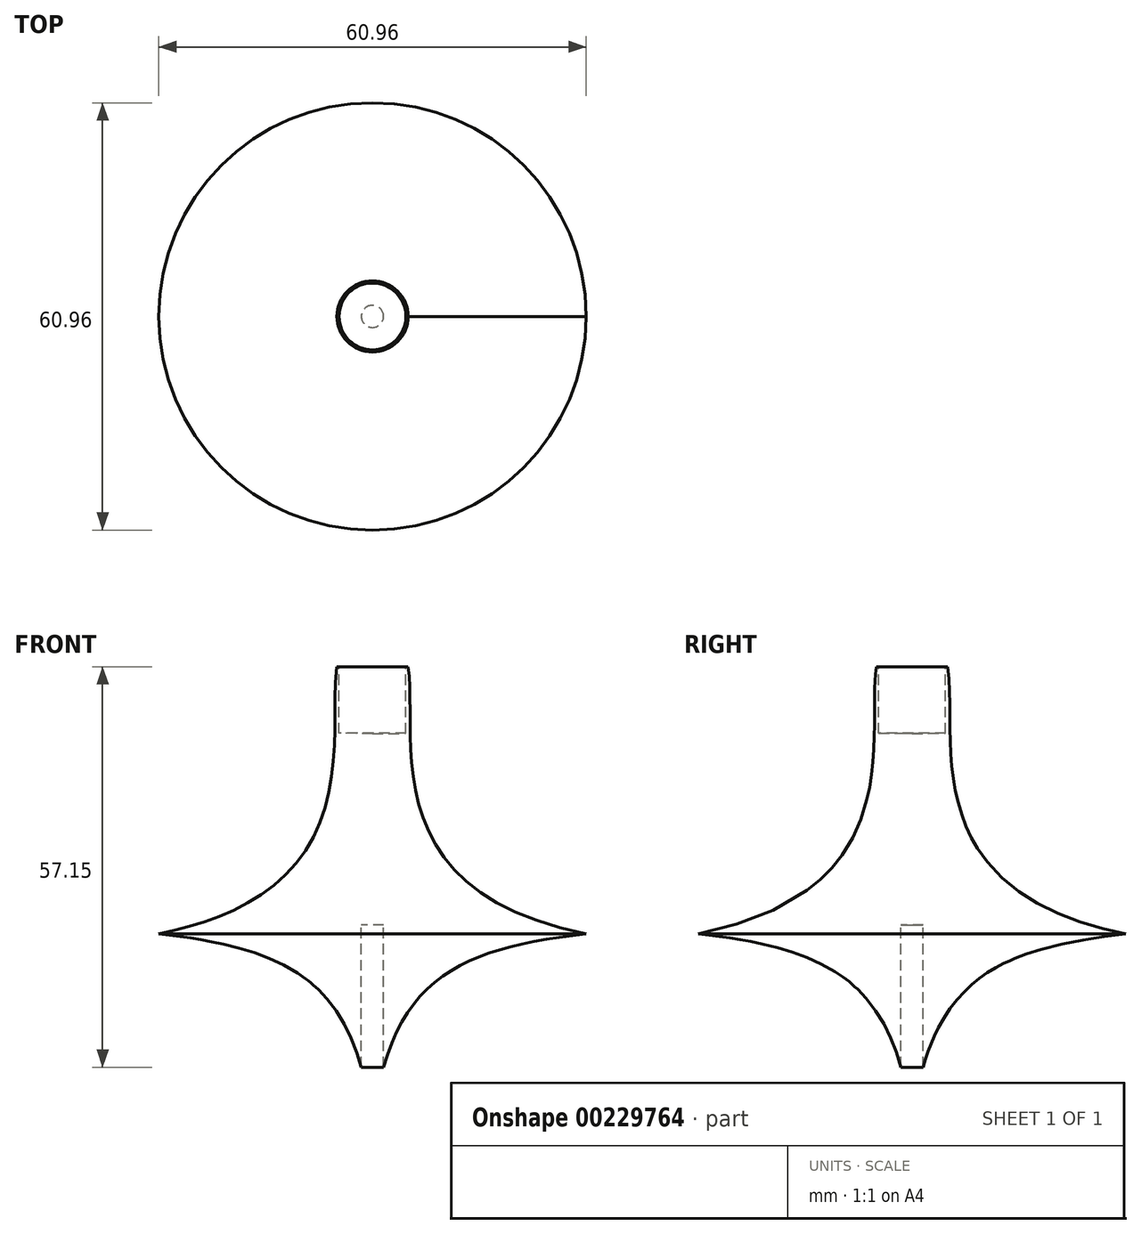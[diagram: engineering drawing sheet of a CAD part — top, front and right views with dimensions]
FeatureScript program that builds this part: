
annotation { "Feature Type Name" : "Feature", "Feature Type Description" : "" }
export const myFeature = defineFeature(function(context is Context, id is Id, definition is map)
    precondition{}
    {
        {
            var Q0;
            Q0=qCreatedBy(makeId("Front.planeOp"),FACE);
            var sketch = newSketch(context, id + "F0", { "sketchPlane" : qUnion([Q0])});
            skLineSegment(sketch, "E0", {"start": v(0, 57.15) * mm, "end": v(0, 0) * mm});
            skFitSpline(sketch, "E1", {"points": [v(5.08, 57.15) * mm, v(30.48, 19.05) * mm], "startDerivative": vector(4.43, -30.47) * mm, "endDerivative": vector(91.44, -18.09) * mm});
            skFitSpline(sketch, "E2", {"points": [v(30.48, 19.05) * mm, v(1.59, 0) * mm], "startDerivative": vector(-45.6, -5.57) * mm, "endDerivative": vector(-11.93, -42.45) * mm});
            skLineSegment(sketch, "E3", {"start": v(1.59, 0) * mm, "end": v(1.59, 20.32) * mm});
            skLineSegment(sketch, "E4", {"start": v(0, 47.63) * mm, "end": v(0, 20.32) * mm});
            skLineSegment(sketch, "E5", {"start": v(0, 20.32) * mm, "end": v(1.59, 20.32) * mm});
            skLineSegment(sketch, "E6", {"start": v(5.08, 57.15) * mm, "end": v(4.76, 57.15) * mm});
            skLineSegment(sketch, "E7", {"start": v(4.76, 57.15) * mm, "end": v(4.76, 47.63) * mm});
            skLineSegment(sketch, "E8", {"start": v(4.76, 47.63) * mm, "end": v(0, 47.63) * mm});
            skFitSpline(sketch, "E9", {"points": [v(-57.3, 42.65) * mm, v(-41.8, 25.74) * mm], "startDerivative": vector(8.35, -25.06) * mm, "endDerivative": vector(31.62, 1.2) * mm});
            skSolve(sketch);
        }
        {
            var Q0;
            Q0 = qSketchRegion(id + "F0", true);
            var Q1;
            Q1=sQuery(id+"F0.wireOp",EDGE,"E0");
            revolve(context, id + "F1", {"entities" : qUnion([Q0]), "axis" : qUnion([Q1]), "revolveType" : RevolveType.FULL});
        }
    });
